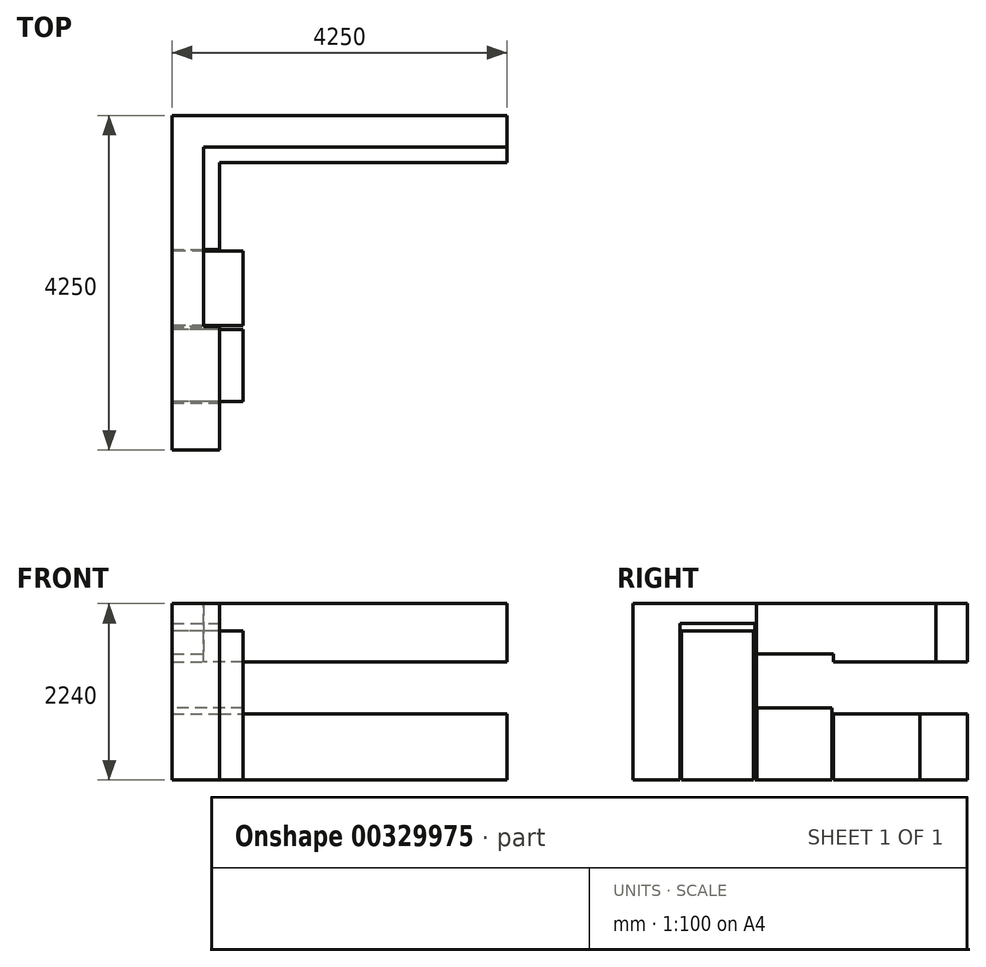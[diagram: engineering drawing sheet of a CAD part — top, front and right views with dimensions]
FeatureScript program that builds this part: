
annotation { "Feature Type Name" : "Feature", "Feature Type Description" : "" }
export const myFeature = defineFeature(function(context is Context, id is Id, definition is map)
    precondition{}
    {
        {
            var Q0;
            Q0=qCreatedBy(makeId("Top.planeOp"),FACE);
            var sketch = newSketch(context, id + "F0", { "sketchPlane" : qUnion([Q0])});
            skLineSegment(sketch, "E0", {"start": v(-600, 600) * mm, "end": v(-600, -3650) * mm});
            skLineSegment(sketch, "E1", {"start": v(-600, -3650) * mm, "end": v(0, -3650) * mm});
            skLineSegment(sketch, "E2", {"start": v(0, -3650) * mm, "end": v(0, 0) * mm});
            skLineSegment(sketch, "E3", {"start": v(0, 0) * mm, "end": v(3650, 0) * mm});
            skLineSegment(sketch, "E4", {"start": v(3650, 0) * mm, "end": v(3650, 600) * mm});
            skLineSegment(sketch, "E5", {"start": v(3650, 600) * mm, "end": v(-600, 600) * mm});
            skSolve(sketch);
        }
        {
            var Q0;
            Q0=makeQuery(id+"F0.imprint","IMPRINT",FACE,{"disambiguationData":[TD([[makeQuery(id+"F0.imprint","IMPRINT",EDGE,{"derivedFrom":sQuery(id+"F0.wireOp",EDGE,"E0")}),1.0]])]});
            extrude(context, id + "F1", {"entities" : qUnion([Q0]), "depth" : 840 * mm});
        }
        {
            var Q0;
            Q0=makeQuery(id+"F1.opExtrude","CAP_FACE",FACE,{"disambiguationData":[OSD([sQuery(id+"F0.wireOp",EDGE,"E0"),sQuery(id+"F0.wireOp",EDGE,"E1"),sQuery(id+"F0.wireOp",EDGE,"E2"),sQuery(id+"F0.wireOp",EDGE,"E3"),sQuery(id+"F0.wireOp",EDGE,"E4"),sQuery(id+"F0.wireOp",EDGE,"E5")])],"isStart":false});
            var sketch = newSketch(context, id + "F2", { "sketchPlane" : qUnion([Q0])});
            skLineSegment(sketch, "E6.bottom", {"start": v(-600, -3650) * mm, "end": v(0, -3650) * mm});
            skLineSegment(sketch, "E6.top", {"start": v(-600, -3050) * mm, "end": v(0, -3050) * mm});
            skLineSegment(sketch, "E6.left", {"start": v(-600, -3650) * mm, "end": v(-600, -3050) * mm});
            skLineSegment(sketch, "E6.right", {"start": v(0, -3650) * mm, "end": v(0, -3050) * mm});
            skSolve(sketch);
        }
        {
            var Q0;
            Q0=makeQuery(id+"F2.imprint","IMPRINT",FACE,{"disambiguationData":[TD([[makeQuery(id+"F2.imprint","IMPRINT",EDGE,{"derivedFrom":sQuery(id+"F2.wireOp",EDGE,"E6.bottom")}),1.0]])]});
            extrude(context, id + "F3", {"entities" : qUnion([Q0]), "operationType" : NewBodyOperationType.ADD, "depth" : 1400 * mm});
        }
        {
            var Q0;
            Q0=makeQuery(id+"F3.boolean.opBoolean","MERGE",FACE,{"derivedFrom":[makeQuery(id+"F1.opExtrude","SWEPT_FACE",FACE,{"disambiguationData":[OSD([sQuery(id+"F0.wireOp",EDGE,"E2")])]}),makeQuery(id+"F3.opExtrude","SWEPT_FACE",FACE,{"disambiguationData":[OSD([sQuery(id+"F2.wireOp",EDGE,"E6.right")])]})]});
            var sketch = newSketch(context, id + "F4", { "sketchPlane" : qUnion([Q0])});
            skLineSegment(sketch, "E7.bottom", {"start": v(-3050, 2240) * mm, "end": v(-2100, 2240) * mm});
            skLineSegment(sketch, "E7.top", {"start": v(-3050, 1990) * mm, "end": v(-2100, 1990) * mm});
            skLineSegment(sketch, "E7.left", {"start": v(-3050, 2240) * mm, "end": v(-3050, 1990) * mm});
            skLineSegment(sketch, "E7.right", {"start": v(-2100, 2240) * mm, "end": v(-2100, 1990) * mm});
            skSolve(sketch);
        }
        {
            var Q0;
            Q0=makeQuery(id+"F4.imprint","IMPRINT",FACE,{"disambiguationData":[TD([[makeQuery(id+"F4.imprint","IMPRINT",EDGE,{"derivedFrom":sQuery(id+"F4.wireOp",EDGE,"E7.bottom")}),-1.0]])]});
            var Q1;
            Q1=makeQuery(id+"F3.boolean.opBoolean","MERGE",FACE,{"derivedFrom":[makeQuery(id+"F1.opExtrude","SWEPT_FACE",FACE,{"disambiguationData":[OSD([sQuery(id+"F0.wireOp",EDGE,"E0")])]}),makeQuery(id+"F3.opExtrude","SWEPT_FACE",FACE,{"disambiguationData":[OSD([sQuery(id+"F2.wireOp",EDGE,"E6.left")])]})]});
            extrude(context, id + "F5", {"entities" : qUnion([Q0]), "operationType" : NewBodyOperationType.ADD, "endBound" : BoundingType.UP_TO_SURFACE, "oppositeDirection" : true, "endBoundEntityFace" : qUnion([Q1]), "depth" : 25 * mm});
        }
        {
            var Q0;
            Q0=makeQuery(id+"F5.boolean.opBoolean","MERGE",FACE,{"derivedFrom":[makeQuery(id+"F3.boolean.opBoolean","MERGE",FACE,{"derivedFrom":[makeQuery(id+"F1.opExtrude","SWEPT_FACE",FACE,{"disambiguationData":[OSD([sQuery(id+"F0.wireOp",EDGE,"E2")])]}),makeQuery(id+"F3.opExtrude","SWEPT_FACE",FACE,{"disambiguationData":[OSD([sQuery(id+"F2.wireOp",EDGE,"E6.right")])]})]}),makeQuery(id+"F5.opExtrude","CAP_FACE",FACE,{"disambiguationData":[OSD([sQuery(id+"F4.wireOp",EDGE,"E7.bottom"),sQuery(id+"F4.wireOp",EDGE,"E7.top"),sQuery(id+"F4.wireOp",EDGE,"E7.left"),sQuery(id+"F4.wireOp",EDGE,"E7.right")])],"isStart":true})]});
            var sketch = newSketch(context, id + "F6", { "sketchPlane" : qUnion([Q0])});
            skLineSegment(sketch, "E8.bottom", {"start": v(-3050, 840) * mm, "end": v(-1100, 840) * mm});
            skLineSegment(sketch, "E8.top", {"start": v(-3050, 0) * mm, "end": v(-1100, 0) * mm});
            skLineSegment(sketch, "E8.left", {"start": v(-3050, 840) * mm, "end": v(-3050, 0) * mm});
            skLineSegment(sketch, "E8.right", {"start": v(-1100, 840) * mm, "end": v(-1100, 0) * mm});
            skSolve(sketch);
        }
        {
            var Q0;
            Q0=makeQuery(id+"F6.imprint","IMPRINT",FACE,{"disambiguationData":[TD([[makeQuery(id+"F6.imprint","IMPRINT",EDGE,{"derivedFrom":sQuery(id+"F6.wireOp",EDGE,"E8.bottom")}),-1.0]])]});
            extrude(context, id + "F7", {"entities" : qUnion([Q0]), "operationType" : NewBodyOperationType.REMOVE, "endBound" : BoundingType.THROUGH_ALL, "oppositeDirection" : true, "depth" : 25 * mm});
        }
        {
            var Q0;
            {var subQ0=sQuery(id+"F2.wireOp",EDGE,"E6.left");var subQ3=sQuery(id+"F0.wireOp",EDGE,"E1");var subQ4=sQuery(id+"F0.wireOp",EDGE,"E0");Q0=makeQuery(id+"F7.boolean.opBoolean","SPLIT",FACE,{"disambiguationData":[TD([makeQuery(id+"F1.opExtrude","SWEPT_FACE",FACE,{"disambiguationData":[OSD([subQ3])]})])],"derivedFrom":makeQuery(id+"F5.boolean.opBoolean","MERGE",FACE,{"derivedFrom":[makeQuery(id+"F3.boolean.opBoolean","MERGE",FACE,{"derivedFrom":[makeQuery(id+"F1.opExtrude","SWEPT_FACE",FACE,{"disambiguationData":[OSD([subQ4])]}),makeQuery(id+"F3.opExtrude","SWEPT_FACE",FACE,{"disambiguationData":[OSD([subQ0])]})]}),makeQuery(id+"F5.opExtrude","CAP_FACE",FACE,{"disambiguationData":[OSD([subQ4,subQ0])],"isStart":false})]})});}
            var sketch = newSketch(context, id + "F8", { "sketchPlane" : qUnion([Q0])});
            skLineSegment(sketch, "E9.bottom", {"start": v(2100, 2240) * mm, "end": v(2080, 2240) * mm});
            skLineSegment(sketch, "E9.top", {"start": v(2100, 0) * mm, "end": v(2080, 0) * mm});
            skLineSegment(sketch, "E9.left", {"start": v(2100, 2240) * mm, "end": v(2100, 0) * mm});
            skLineSegment(sketch, "E9.right", {"start": v(2080, 2240) * mm, "end": v(2080, 0) * mm});
            skSolve(sketch);
        }
        {
            var Q0;
            {var subQ1=sQuery(id+"F8.wireOp",EDGE,"E9.bottom");Q0=makeQuery(id+"F8.imprint","IMPRINT",FACE,{"disambiguationData":[TD([[makeQuery(id+"F8.imprint","IMPRINT",EDGE,{"derivedFrom":subQ1}),1.0]])]});}
            var Q1;
            {var subQ0=sQuery(id+"F2.wireOp",EDGE,"E6.right");var subQ3=sQuery(id+"F0.wireOp",EDGE,"E1");var subQ4=sQuery(id+"F0.wireOp",EDGE,"E2");var subQ5=sQuery(id+"F4.wireOp",EDGE,"E7.bottom");var subQ6=sQuery(id+"F4.wireOp",EDGE,"E7.top");var subQ7=sQuery(id+"F4.wireOp",EDGE,"E7.right");Q1=makeQuery(id+"F7.boolean.opBoolean","SPLIT",FACE,{"disambiguationData":[TD([makeQuery(id+"F1.opExtrude","SWEPT_FACE",FACE,{"disambiguationData":[OSD([subQ3])]})])],"derivedFrom":makeQuery(id+"F5.boolean.opBoolean","MERGE",FACE,{"derivedFrom":[makeQuery(id+"F3.boolean.opBoolean","MERGE",FACE,{"derivedFrom":[makeQuery(id+"F1.opExtrude","SWEPT_FACE",FACE,{"disambiguationData":[OSD([subQ4])]}),makeQuery(id+"F3.opExtrude","SWEPT_FACE",FACE,{"disambiguationData":[OSD([subQ0])]})]}),makeQuery(id+"F5.opExtrude","CAP_FACE",FACE,{"disambiguationData":[OSD([subQ5,subQ6,sQuery(id+"F4.wireOp",EDGE,"E7.left"),subQ7])],"isStart":true})]})});}
            extrude(context, id + "F9", {"entities" : qUnion([Q0]), "operationType" : NewBodyOperationType.ADD, "endBound" : BoundingType.UP_TO_SURFACE, "oppositeDirection" : true, "endBoundEntityFace" : qUnion([Q1]), "depth" : 25 * mm});
        }
        {
            var Q0;
            {var subQ0=sQuery(id+"F2.wireOp",EDGE,"E6.left");var subQ3=sQuery(id+"F0.wireOp",EDGE,"E1");var subQ4=sQuery(id+"F0.wireOp",EDGE,"E0");Q0=makeQuery(id+"F9.boolean.opBoolean","MERGE",FACE,{"derivedFrom":[makeQuery(id+"F7.boolean.opBoolean","SPLIT",FACE,{"disambiguationData":[TD([makeQuery(id+"F1.opExtrude","SWEPT_FACE",FACE,{"disambiguationData":[OSD([subQ3])]})])],"derivedFrom":makeQuery(id+"F5.boolean.opBoolean","MERGE",FACE,{"derivedFrom":[makeQuery(id+"F3.boolean.opBoolean","MERGE",FACE,{"derivedFrom":[makeQuery(id+"F1.opExtrude","SWEPT_FACE",FACE,{"disambiguationData":[OSD([subQ4])]}),makeQuery(id+"F3.opExtrude","SWEPT_FACE",FACE,{"disambiguationData":[OSD([subQ0])]})]}),makeQuery(id+"F5.opExtrude","CAP_FACE",FACE,{"disambiguationData":[OSD([subQ4,subQ0])],"isStart":false})]})}),makeQuery(id+"F9.opExtrude","CAP_FACE",FACE,{"disambiguationData":[OSD([sQuery(id+"F8.wireOp",EDGE,"E9.bottom"),sQuery(id+"F8.wireOp",EDGE,"E9.top"),sQuery(id+"F8.wireOp",EDGE,"E9.left"),sQuery(id+"F8.wireOp",EDGE,"E9.right")])],"isStart":true})]});}
            var sketch = newSketch(context, id + "F10", { "sketchPlane" : qUnion([Q0])});
            skLineSegment(sketch, "E10.bottom", {"start": v(2080, 2240) * mm, "end": v(-600, 2240) * mm});
            skLineSegment(sketch, "E10.top", {"start": v(2080, 1500) * mm, "end": v(-600, 1500) * mm});
            skLineSegment(sketch, "E10.left", {"start": v(2080, 2240) * mm, "end": v(2080, 1500) * mm});
            skLineSegment(sketch, "E10.right", {"start": v(-600, 2240) * mm, "end": v(-600, 1500) * mm});
            skSolve(sketch);
        }
        {
            var Q0;
            Q0=makeQuery(id+"F10.imprint","IMPRINT",FACE,{"disambiguationData":[TD([[makeQuery(id+"F10.imprint","IMPRINT",EDGE,{"derivedFrom":sQuery(id+"F10.wireOp",EDGE,"E10.bottom")}),1.0]])]});
            extrude(context, id + "F11", {"entities" : qUnion([Q0]), "operationType" : NewBodyOperationType.ADD, "oppositeDirection" : true, "depth" : 400 * mm});
        }
        {
            var Q0;
            Q0=makeQuery(id+"F11.boolean.opBoolean","MERGE",FACE,{"derivedFrom":[makeQuery(id+"F9.boolean.opBoolean","MERGE",FACE,{"derivedFrom":[makeQuery(id+"F5.boolean.opBoolean","MERGE",FACE,{"derivedFrom":[makeQuery(id+"F3.opExtrude","CAP_FACE",FACE,{"disambiguationData":[OSD([sQuery(id+"F2.wireOp",EDGE,"E6.bottom"),sQuery(id+"F2.wireOp",EDGE,"E6.top"),sQuery(id+"F2.wireOp",EDGE,"E6.left"),sQuery(id+"F2.wireOp",EDGE,"E6.right")])],"isStart":false}),makeQuery(id+"F5.opExtrude","SWEPT_FACE",FACE,{"disambiguationData":[OSD([sQuery(id+"F4.wireOp",EDGE,"E7.bottom")])]})]}),makeQuery(id+"F9.opExtrude","SWEPT_FACE",FACE,{"disambiguationData":[OSD([sQuery(id+"F8.wireOp",EDGE,"E9.bottom")])]})]}),makeQuery(id+"F11.opExtrude","SWEPT_FACE",FACE,{"disambiguationData":[OSD([sQuery(id+"F10.wireOp",EDGE,"E10.bottom")])]})]});
            var sketch = newSketch(context, id + "F12", { "sketchPlane" : qUnion([Q0])});
            skLineSegment(sketch, "E11.bottom", {"start": v(-600, 600) * mm, "end": v(3650, 600) * mm});
            skLineSegment(sketch, "E11.top", {"start": v(-600, 200) * mm, "end": v(3650, 200) * mm});
            skLineSegment(sketch, "E11.left", {"start": v(-600, 600) * mm, "end": v(-600, 200) * mm});
            skLineSegment(sketch, "E11.right", {"start": v(3650, 600) * mm, "end": v(3650, 200) * mm});
            skSolve(sketch);
        }
        {
            var Q0;
            {var subQ3=sQuery(id+"F12.wireOp",EDGE,"E11.right");Q0=makeQuery(id+"F12.imprint","IMPRINT",FACE,{"disambiguationData":[TD([[makeQuery(id+"F12.imprint","IMPRINT",EDGE,{"derivedFrom":subQ3}),-1.0]])]});}
            var Q1;
            Q1=makeQuery(id+"F11.opExtrude","SWEPT_FACE",FACE,{"disambiguationData":[OSD([sQuery(id+"F10.wireOp",EDGE,"E10.top")])]});
            extrude(context, id + "F13", {"entities" : qUnion([Q0]), "operationType" : NewBodyOperationType.ADD, "endBound" : BoundingType.UP_TO_SURFACE, "oppositeDirection" : true, "endBoundEntityFace" : qUnion([Q1]), "depth" : 25 * mm});
        }
        {
            var Q0;
            Q0=makeQuery(id+"F11.opExtrude","CAP_FACE",FACE,{"disambiguationData":[OSD([sQuery(id+"F10.wireOp",EDGE,"E10.bottom"),sQuery(id+"F10.wireOp",EDGE,"E10.top"),sQuery(id+"F10.wireOp",EDGE,"E10.left"),sQuery(id+"F10.wireOp",EDGE,"E10.right")])],"isStart":false});
            var sketch = newSketch(context, id + "F14", { "sketchPlane" : qUnion([Q0])});
            skLineSegment(sketch, "E12.bottom", {"start": v(-2080, 1500) * mm, "end": v(-1100, 1500) * mm});
            skLineSegment(sketch, "E12.top", {"start": v(-2080, 1600) * mm, "end": v(-1100, 1600) * mm});
            skLineSegment(sketch, "E12.left", {"start": v(-2080, 1500) * mm, "end": v(-2080, 1600) * mm});
            skLineSegment(sketch, "E12.right", {"start": v(-1100, 1500) * mm, "end": v(-1100, 1600) * mm});
            skSolve(sketch);
        }
        {
            var Q0;
            Q0=makeQuery(id+"F14.imprint","IMPRINT",FACE,{"disambiguationData":[TD([[makeQuery(id+"F14.imprint","IMPRINT",EDGE,{"derivedFrom":sQuery(id+"F14.wireOp",EDGE,"E12.bottom")}),1.0]])]});
            extrude(context, id + "F15", {"entities" : qUnion([Q0]), "operationType" : NewBodyOperationType.REMOVE, "endBound" : BoundingType.THROUGH_ALL, "oppositeDirection" : true, "depth" : 25 * mm});
        }
        {
            var Q0;
            {var subQ0=sQuery(id+"F2.wireOp",EDGE,"E6.left");var subQ3=sQuery(id+"F0.wireOp",EDGE,"E1");var subQ4=sQuery(id+"F0.wireOp",EDGE,"E0");Q0=makeQuery(id+"F11.boolean.opBoolean","MERGE",FACE,{"derivedFrom":[makeQuery(id+"F9.boolean.opBoolean","MERGE",FACE,{"derivedFrom":[makeQuery(id+"F7.boolean.opBoolean","SPLIT",FACE,{"disambiguationData":[TD([makeQuery(id+"F1.opExtrude","SWEPT_FACE",FACE,{"disambiguationData":[OSD([subQ3])]})])],"derivedFrom":makeQuery(id+"F5.boolean.opBoolean","MERGE",FACE,{"derivedFrom":[makeQuery(id+"F3.boolean.opBoolean","MERGE",FACE,{"derivedFrom":[makeQuery(id+"F1.opExtrude","SWEPT_FACE",FACE,{"disambiguationData":[OSD([subQ4])]}),makeQuery(id+"F3.opExtrude","SWEPT_FACE",FACE,{"disambiguationData":[OSD([subQ0])]})]}),makeQuery(id+"F5.opExtrude","CAP_FACE",FACE,{"disambiguationData":[OSD([subQ4,subQ0])],"isStart":false})]})}),makeQuery(id+"F9.opExtrude","CAP_FACE",FACE,{"disambiguationData":[OSD([sQuery(id+"F8.wireOp",EDGE,"E9.bottom"),sQuery(id+"F8.wireOp",EDGE,"E9.top"),sQuery(id+"F8.wireOp",EDGE,"E9.left"),sQuery(id+"F8.wireOp",EDGE,"E9.right")])],"isStart":true})]}),makeQuery(id+"F11.opExtrude","CAP_FACE",FACE,{"disambiguationData":[OSD([sQuery(id+"F10.wireOp",EDGE,"E10.bottom"),sQuery(id+"F10.wireOp",EDGE,"E10.top"),sQuery(id+"F10.wireOp",EDGE,"E10.left"),sQuery(id+"F10.wireOp",EDGE,"E10.right")])],"isStart":true})]});}
            var sketch = newSketch(context, id + "F16", { "sketchPlane" : qUnion([Q0])});
            skLineSegment(sketch, "E13.bottom", {"start": v(3030, 0) * mm, "end": v(2120, 0) * mm});
            skLineSegment(sketch, "E13.top", {"start": v(3030, 1890) * mm, "end": v(2120, 1890) * mm});
            skLineSegment(sketch, "E13.left", {"start": v(3030, 0) * mm, "end": v(3030, 1890) * mm});
            skLineSegment(sketch, "E13.right", {"start": v(2120, 0) * mm, "end": v(2120, 1890) * mm});
            skPoint(sketch, "E14.firstSnap0", {"position": v(2575, 0) * mm});
            skLineSegment(sketch, "E14.bottom", {"start": v(2070, 0) * mm, "end": v(1120, 0) * mm});
            skLineSegment(sketch, "E14.top", {"start": v(2070, 916.58) * mm, "end": v(1120, 916.58) * mm});
            skLineSegment(sketch, "E14.left", {"start": v(2070, 0) * mm, "end": v(2070, 916.58) * mm});
            skLineSegment(sketch, "E14.right", {"start": v(1120, 0) * mm, "end": v(1120, 916.58) * mm});
            skSolve(sketch);
        }
        {
            var Q0;
            Q0=makeQuery(id+"F16.imprint","IMPRINT",FACE,{"disambiguationData":[TD([[makeQuery(id+"F16.imprint","IMPRINT",EDGE,{"derivedFrom":sQuery(id+"F16.wireOp",EDGE,"E13.bottom")}),-1.0]])]});
            var Q1;
            Q1=makeQuery(id+"F16.imprint","IMPRINT",FACE,{"disambiguationData":[TD([[makeQuery(id+"F16.imprint","IMPRINT",EDGE,{"derivedFrom":sQuery(id+"F16.wireOp",EDGE,"E14.bottom")}),-1.0]])]});
            extrude(context, id + "F17", {"entities" : qUnion([Q0, Q1]), "oppositeDirection" : true, "depth" : 900 * mm});
        }
    });
